# Revit family: ARKOSLIGHT_Track 1L Surface
name_source: partatom
category: Lighting Fixtures
units: mm (PartAtom-declared; Revit-internal decimal feet)

## family parameters
Cut with Voids When Loaded = No
Host = Face
Light Source = No
Part Type = Normal
Room Calculation Point = No
Round Connector Dimension = Use Diameter
Shared = No

## types (2) — shared parameters
ARKOSLIGHT_Dimming = No
ARKOSLIGHT_Fixture Type = ACCESSORIES
ARKOSLIGHT_Model = ACCESSORIES
ARKOSLIGHT_Series = ACCESORIOS TRACK 1L
Apparent Load = 0 VA
Description = Select the number and length of profiles suitable for the defined length
Manufacturer = ARKOSLIGHT
Model = ACCESSORIES
URL = https://www.arkoslight.com
zero-valued in all types: Default Elevation

## per-type parameters (varying)
| type | ARKOSLIGHT_Body Color | ARKOSLIGHT_Color | ARKOSLIGHT_Reference |
| A2640X00B - TRACK 1L SURFACE XM B | ARKOSLIGHT_White | White | A2640X00B |
| A2640X00N - TRACK 1L SURFACE XM N | ARKOSLIGHT_Black | Black | A2640X00N |

## geometry (parser evidence)
native form markers: Sweep x2
no freeform markers — native parametric forms only
